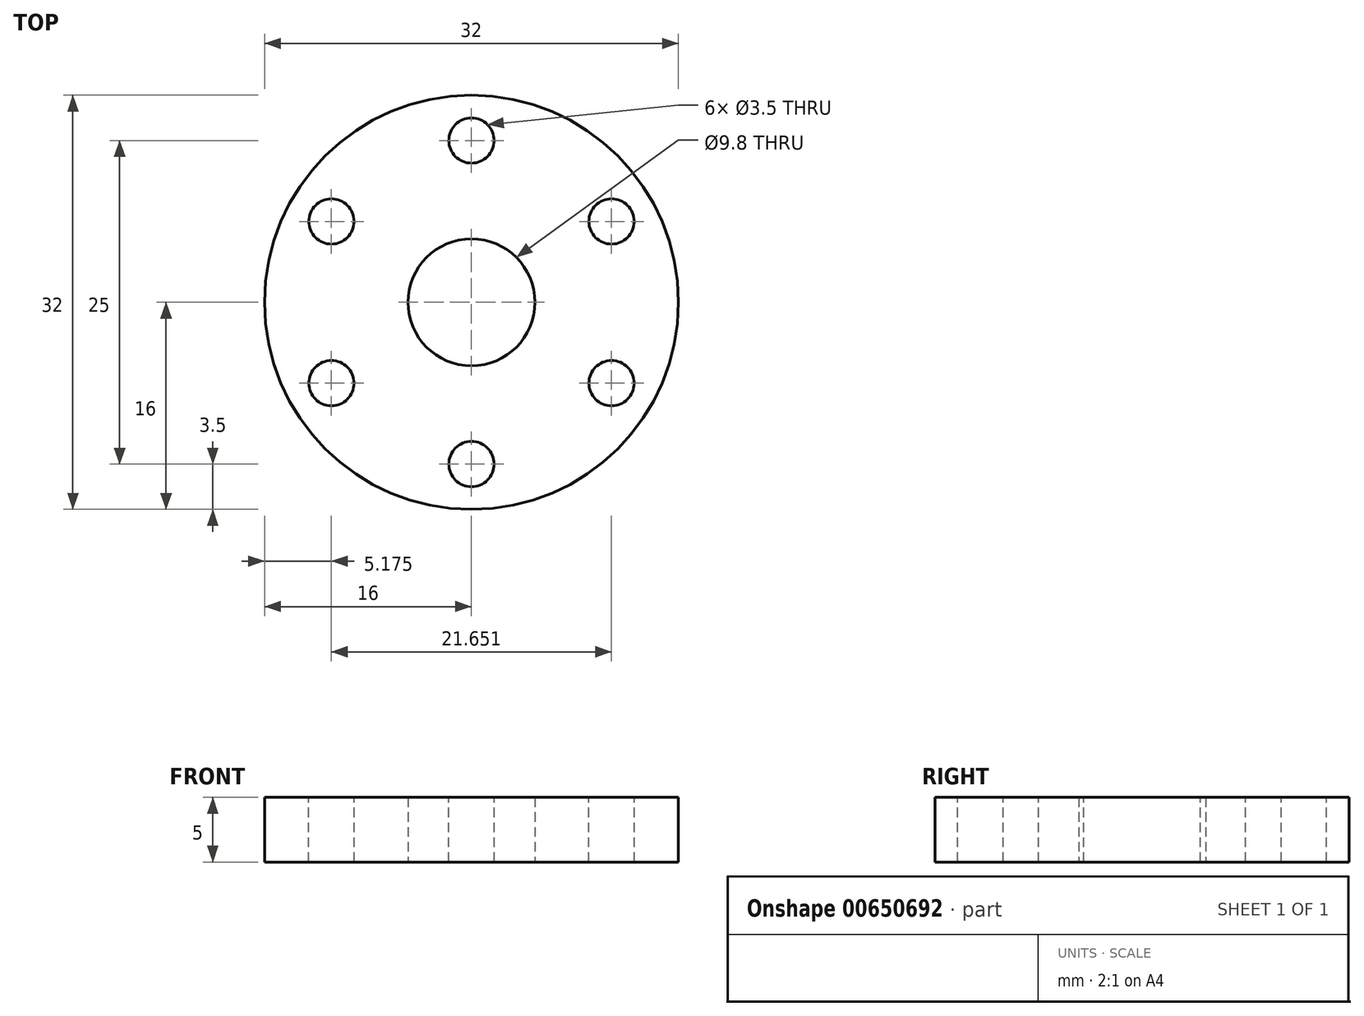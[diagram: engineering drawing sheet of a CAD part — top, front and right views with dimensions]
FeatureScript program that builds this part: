
annotation { "Feature Type Name" : "Feature", "Feature Type Description" : "" }
export const myFeature = defineFeature(function(context is Context, id is Id, definition is map)
    precondition{}
    {
        {
            var Q0;
            Q0=qCreatedBy(makeId("Top.planeOp"),FACE);
            var sketch = newSketch(context, id + "F0", { "sketchPlane" : qUnion([Q0])});
            skCircle(sketch, "E0", {"center": v(0, 0) * mm, "radius": 16 * mm});
            skCircle(sketch, "E1", {"center": v(0, 0) * mm, "radius": 4.9 * mm});
            skSolve(sketch);
        }
        {
            var Q0;
            Q0=makeQuery(id+"F0.imprint","IMPRINT",FACE,{"disambiguationData":[TD([[makeQuery(id+"F0.imprint","IMPRINT",EDGE,{"derivedFrom":sQuery(id+"F0.wireOp",EDGE,"E0")}),1.0]])]});
            extrude(context, id + "F1", {"entities" : qUnion([Q0]), "depth" : 5 * mm, "offsetDistance" : 25 * mm});
        }
        {
            var Q0;
            Q0=makeQuery(id+"F1.opExtrude","CAP_FACE",FACE,{"disambiguationData":[OSD([sQuery(id+"F0.wireOp",EDGE,"E0"),sQuery(id+"F0.wireOp",EDGE,"E1")])],"isStart":false});
            var sketch = newSketch(context, id + "F2", { "sketchPlane" : qUnion([Q0])});
            skCircle(sketch, "E2.cCircle", {"center": v(0, 0) * mm, "radius": 12.5 * mm, "construction": true});
            skLineSegment(sketch, "E2.0", {"start": v(0, 12.5) * mm, "end": v(10.83, 6.25) * mm, "construction": true});
            skLineSegment(sketch, "E2.1", {"start": v(10.83, 6.25) * mm, "end": v(10.83, -6.25) * mm, "construction": true});
            skLineSegment(sketch, "E2.2", {"start": v(10.83, -6.25) * mm, "end": v(0, -12.5) * mm, "construction": true});
            skLineSegment(sketch, "E2.3", {"start": v(0, -12.5) * mm, "end": v(-10.83, -6.25) * mm, "construction": true});
            skLineSegment(sketch, "E2.4", {"start": v(-10.83, -6.25) * mm, "end": v(-10.83, 6.25) * mm, "construction": true});
            skLineSegment(sketch, "E2.5", {"start": v(-10.83, 6.25) * mm, "end": v(0, 12.5) * mm, "construction": true});
            skCircle(sketch, "E3", {"center": v(0, 12.5) * mm, "radius": 1.75 * mm});
            skCircle(sketch, "E4", {"center": v(10.83, 6.25) * mm, "radius": 1.75 * mm});
            skCircle(sketch, "E5", {"center": v(10.83, -6.25) * mm, "radius": 1.75 * mm});
            skCircle(sketch, "E6", {"center": v(0, -12.5) * mm, "radius": 1.75 * mm});
            skCircle(sketch, "E7", {"center": v(-10.83, -6.25) * mm, "radius": 1.75 * mm});
            skCircle(sketch, "E8", {"center": v(-10.83, 6.25) * mm, "radius": 1.75 * mm});
            skSolve(sketch);
        }
        {
            var Q0;
            Q0 = qSketchRegion(id + "F2", true);
            extrude(context, id + "F3", {"entities" : qUnion([Q0]), "operationType" : NewBodyOperationType.REMOVE, "oppositeDirection" : true, "depth" : 25 * mm, "offsetDistance" : 25 * mm});
        }
    });
